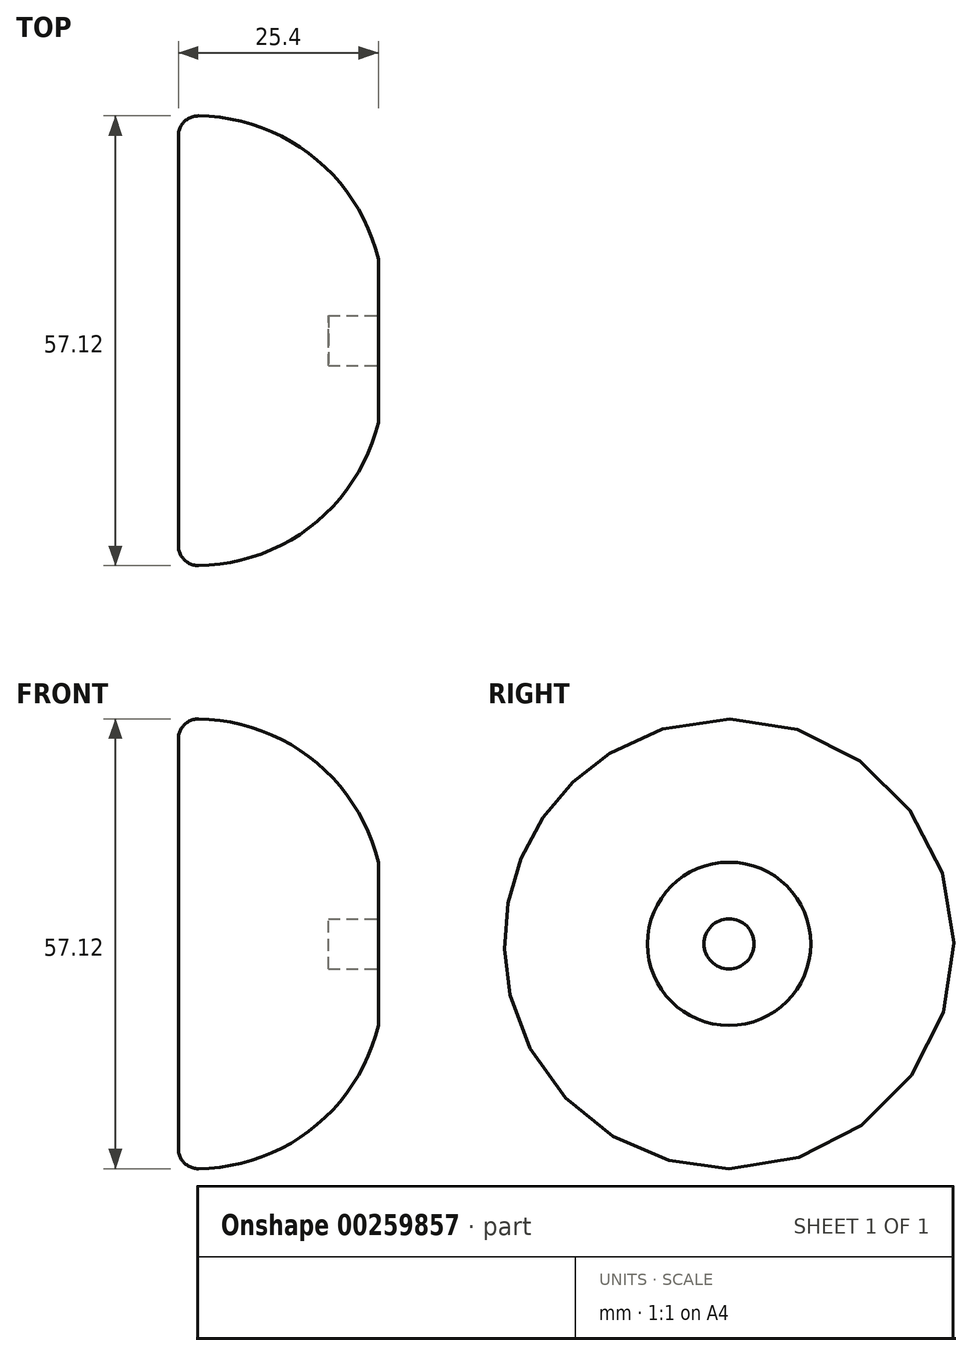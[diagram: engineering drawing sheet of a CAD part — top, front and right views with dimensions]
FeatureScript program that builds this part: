
annotation { "Feature Type Name" : "Feature", "Feature Type Description" : "" }
export const myFeature = defineFeature(function(context is Context, id is Id, definition is map)
    precondition{}
    {
        {
            var Q0;
            Q0=qCreatedBy(makeId("Front.planeOp"),FACE);
            var sketch = newSketch(context, id + "F0", { "sketchPlane" : qUnion([Q0])});
            skLineSegment(sketch, "E0", {"start": v(22.55, 28.45) * mm, "end": v(22.55, 0) * mm});
            skLineSegment(sketch, "E1", {"start": v(47.95, 10.37) * mm, "end": v(47.95, 0) * mm});
            skArc(sketch, "E2", {"start": v(47.95, 10.37) * mm, "mid": v(38.64, 24.16) * mm, "end": v(22.55, 28.45) * mm});
            skLineSegment(sketch, "E3", {"start": v(22.55, 0) * mm, "end": v(47.95, 0) * mm});
            skSolve(sketch);
        }
        {
            var Q0;
            Q0=qCreatedBy(makeId("Front.planeOp"),FACE);
            var sketch = newSketch(context, id + "F1", { "sketchPlane" : qUnion([Q0])});
            skLineSegment(sketch, "E4", {"start": v(0, 0) * mm, "end": v(78.57, 0) * mm});
            skSolve(sketch);
        }
        {
            var Q0;
            Q0=makeQuery(id+"F0.imprint","IMPRINT",FACE,{"disambiguationData":[TD([[makeQuery(id+"F0.imprint","IMPRINT",EDGE,{"derivedFrom":sQuery(id+"F0.wireOp",EDGE,"E0")}),1.0]])]});
            var Q1;
            Q1=sQuery(id+"F1.wireOp",EDGE,"E4");
            revolve(context, id + "F2", {"entities" : qUnion([Q0]), "axis" : qUnion([Q1]), "revolveType" : RevolveType.FULL});
        }
        {
            var Q0;
            Q0=makeQuery(id+"F2.opRevolve","SWEPT_EDGE",EDGE,{"disambiguationData":[OSD([sQuery(id+"F0.wireOp",EDGE,"E0"),sQuery(id+"F0.wireOp",EDGE,"E2")])]});
            fillet(context, id + "F3", {"entities" : qUnion([Q0]), "radius" : 2.54 * mm, "tangentPropagation" : true, "allowEdgeOverflow" : false});
        }
        {
            var Q0;
            Q0=makeQuery(id+"F2.opRevolve","SWEPT_FACE",FACE,{"disambiguationData":[OSD([sQuery(id+"F0.wireOp",EDGE,"E1")])]});
            var sketch = newSketch(context, id + "F4", { "sketchPlane" : qUnion([Q0])});
            skCircle(sketch, "E5", {"center": v(0, 0) * mm, "radius": 3.18 * mm});
            skSolve(sketch);
        }
        {
            var Q0;
            Q0 = qSketchRegion(id + "F4", true);
            extrude(context, id + "F5", {"entities" : qUnion([Q0]), "operationType" : NewBodyOperationType.REMOVE, "oppositeDirection" : true, "depth" : 6.35 * mm});
        }
    });
